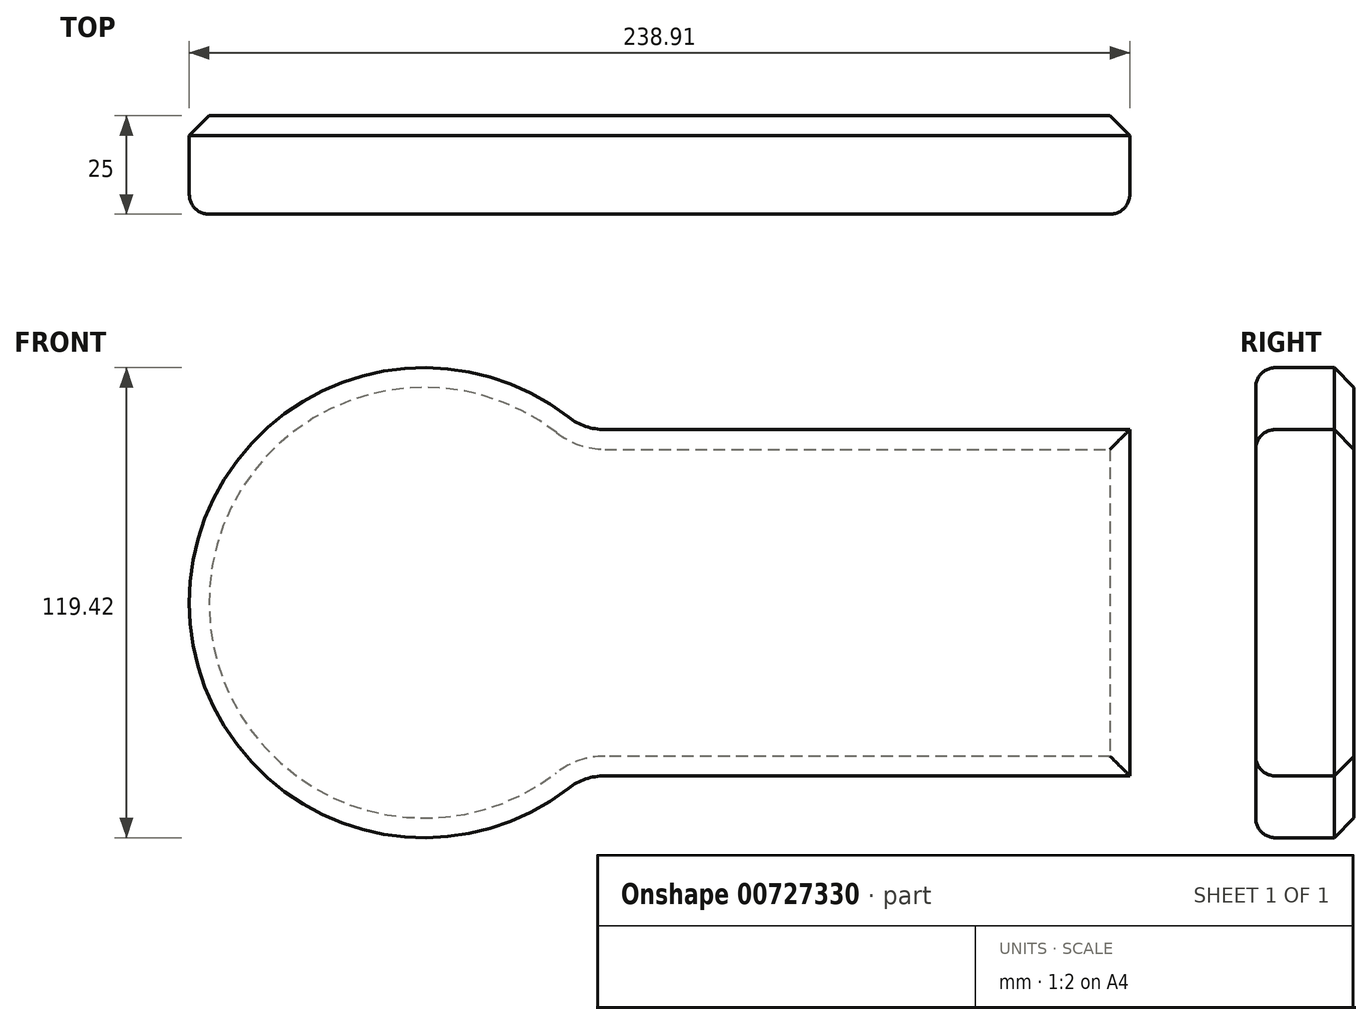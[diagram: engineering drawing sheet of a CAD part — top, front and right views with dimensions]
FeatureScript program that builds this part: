
annotation { "Feature Type Name" : "Feature", "Feature Type Description" : "" }
export const myFeature = defineFeature(function(context is Context, id is Id, definition is map)
    precondition{}
    {
        {
            var Q0;
            Q0=qCreatedBy(makeId("Front.planeOp"),FACE);
            var sketch = newSketch(context, id + "F0", { "sketchPlane" : qUnion([Q0])});
            skLineSegment(sketch, "E0.bottom", {"start": v(-104.26, 51.23) * mm, "end": v(74.95, 51.23) * mm});
            skLineSegment(sketch, "E0.top", {"start": v(-104.26, -36.75) * mm, "end": v(74.95, -36.75) * mm});
            skLineSegment(sketch, "E0.left", {"start": v(-104.26, 51.23) * mm, "end": v(-104.26, -36.75) * mm});
            skLineSegment(sketch, "E0.right", {"start": v(74.95, 51.23) * mm, "end": v(74.95, -36.75) * mm});
            skSolve(sketch);
        }
        {
            var Q0;
            Q0=makeQuery(id+"F0.imprint","IMPRINT",FACE,{"disambiguationData":[TD([[makeQuery(id+"F0.imprint","IMPRINT",EDGE,{"derivedFrom":sQuery(id+"F0.wireOp",EDGE,"E0.bottom")}),-1.0]])]});
            extrude(context, id + "F1", {"entities" : qUnion([Q0]), "depth" : 25 * mm, "offsetDistance" : 25 * mm});
        }
        {
            var Q0;
            Q0=makeQuery(id+"F1.opExtrude","CAP_FACE",FACE,{"disambiguationData":[OSD([sQuery(id+"F0.wireOp",EDGE,"E0.bottom"),sQuery(id+"F0.wireOp",EDGE,"E0.top"),sQuery(id+"F0.wireOp",EDGE,"E0.left"),sQuery(id+"F0.wireOp",EDGE,"E0.right")])],"isStart":false});
            var sketch = newSketch(context, id + "F2", { "sketchPlane" : qUnion([Q0])});
            skCircle(sketch, "E1", {"center": v(-104.26, 7.24) * mm, "radius": 59.7 * mm});
            skSolve(sketch);
        }
        {
            var Q0;
            Q0 = qSketchRegion(id + "F2", true);
            var Q1;
            Q1=makeQuery(id+"F1.opExtrude","CAP_FACE",FACE,{"disambiguationData":[OSD([sQuery(id+"F0.wireOp",EDGE,"E0.bottom"),sQuery(id+"F0.wireOp",EDGE,"E0.top"),sQuery(id+"F0.wireOp",EDGE,"E0.left"),sQuery(id+"F0.wireOp",EDGE,"E0.right")])],"isStart":true});
            extrude(context, id + "F3", {"entities" : qUnion([Q0]), "operationType" : NewBodyOperationType.ADD, "endBound" : BoundingType.UP_TO_SURFACE, "oppositeDirection" : true, "depth" : -50 * mm, "endBoundEntityFace" : qUnion([Q1]), "offsetDistance" : 25 * mm});
        }
        {
            var Q0;
            Q0=makeQuery(id+"F3.boolean.opBoolean","INTERSECT",EDGE,{"derivedFrom":[makeQuery(id+"F1.opExtrude","SWEPT_FACE",FACE,{"disambiguationData":[OSD([sQuery(id+"F0.wireOp",EDGE,"E0.bottom")])]}),makeQuery(id+"F3.opExtrude","SWEPT_FACE",FACE,{"disambiguationData":[OSD([sQuery(id+"F2.wireOp",EDGE,"E1")])]})]});
            var Q1;
            Q1=makeQuery(id+"F3.boolean.opBoolean","INTERSECT",EDGE,{"derivedFrom":[makeQuery(id+"F1.opExtrude","SWEPT_FACE",FACE,{"disambiguationData":[OSD([sQuery(id+"F0.wireOp",EDGE,"E0.top")])]}),makeQuery(id+"F3.opExtrude","SWEPT_FACE",FACE,{"disambiguationData":[OSD([sQuery(id+"F2.wireOp",EDGE,"E1")])]})]});
            fillet(context, id + "F4", {"entities" : qUnion([Q0, Q1]), "radius" : 15 * mm, "tangentPropagation" : true, "allowEdgeOverflow" : false});
        }
        {
            var Q0;
            Q0=makeQuery(id+"F3.boolean.opBoolean","MERGE",FACE,{"derivedFrom":[makeQuery(id+"F1.opExtrude","CAP_FACE",FACE,{"disambiguationData":[OSD([sQuery(id+"F0.wireOp",EDGE,"E0.bottom"),sQuery(id+"F0.wireOp",EDGE,"E0.top"),sQuery(id+"F0.wireOp",EDGE,"E0.left"),sQuery(id+"F0.wireOp",EDGE,"E0.right")])],"isStart":false}),makeQuery(id+"F3.opExtrude","CAP_FACE",FACE,{"disambiguationData":[OSD([sQuery(id+"F2.wireOp",EDGE,"E1")])],"isStart":true})]});
            fillet(context, id + "F5", {"entities" : qUnion([Q0]), "radius" : 5 * mm, "tangentPropagation" : true, "allowEdgeOverflow" : false});
        }
        {
            var Q0;
            {var subQ0=sQuery(id+"F0.wireOp",EDGE,"E0.right");var subQ1=sQuery(id+"F0.wireOp",EDGE,"E0.left");var subQ2=sQuery(id+"F0.wireOp",EDGE,"E0.top");var subQ3=sQuery(id+"F0.wireOp",EDGE,"E0.bottom");Q0=makeQuery(id+"F3.boolean.opBoolean","MERGE",FACE,{"derivedFrom":[makeQuery(id+"F1.opExtrude","CAP_FACE",FACE,{"disambiguationData":[OSD([subQ3,subQ2,subQ1,subQ0])],"isStart":true}),makeQuery(id+"F3.opExtrude","CAP_FACE",FACE,{"disambiguationData":[OSD([subQ3,subQ2,subQ1,subQ0])],"isStart":false})]});}
            chamfer(context, id + "F6", {"entities" : qUnion([Q0]), "width" : 5 * mm, "tangentPropagation" : true});
        }
    });
